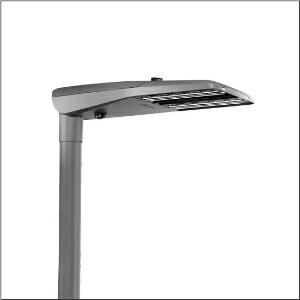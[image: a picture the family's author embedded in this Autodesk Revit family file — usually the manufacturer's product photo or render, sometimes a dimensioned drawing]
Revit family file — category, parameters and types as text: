
# Revit family: streetlight_sl_11_iq_midi___st1_2a_5xc3a61y08me_9d9d
name_source: partatom
category: Lighting Fixtures
units: mm (PartAtom-declared; Revit-internal decimal feet)

## family parameters
Cut with Voids When Loaded = No
Host = Face
Light Source = No
Part Type = Normal
Room Calculation Point = No
Round Connector Dimension = Use Diameter
Shared = No

## types (1)
- --- (1 x LED, 16240 lm, 122.7 W, 2700K)
    Apparent Load = 123 VA
    CIE Flux Codes = 32 70 96 100 100
    Color Rendering = 70
    Color Temperature = 2700K
    Default Elevation = 1800 mm
    Description = Streetlight SL 11 iQ midi, mast luminaire, primary light control with 3 zone facetted reflector, of plastic, silver coated, highly specular, primary optical cover: cover, of PMMA, transparent, light distribution: ST1.2a, light emission: direct distribution, primary light characteristic: asymmetric, installation type: post-top, side-entry, LED, High Power LED, rated luminous flux: 16.240lm, luminous efficacy: 132lm/W, light colour: 727, colour temperature: 2700K, control: presetting dimming logarithmic, Street-Remote, Auto-Match, Temp-Guard, Lumen-Switch, Night-Set, Smart-Wire, Light-Fading, Desk-Remote (wireless, voltage-free reading and setting of iQ features in the workshop via application-optimized NFC function/RFID function), optimised constant luminous flux control (CLO 2.0), with cable H07RN-F 5x 1.5mm², mains connection: 230..240V, AC, 50/60Hz, connection cable pre-assembled, cable length: 12,5m, start of lifetime: 123W, end of service life: 130W, reduction: 56W, luminaire housing, of diecast aluminium, powder-coated, Siteco® metallic grey (DB 702S), please order mast flange separately, inclination adjustable without tools: 0°, 5°, 10°, 15° (post-top) | 0°, -5°, -10°, -15° (side-entry), sealing non-destructively replaceable, multi-level sealing system, length: 780mm, width: 376mm, height: 118mm, mast flange for spigot size: 42mm (side-entry): 5XC10008XM4, 60/48mm (side-entry/post-top): 5XC10108XM2, 76/60mm (side-entry/post-top): 5XC10108XM1, equipment: Power, Smart Interface below and above, protection rating (complete): IP66, insulation class (complete): insulation class II (safety insulation), certification: CE, ENEC, VDE, UKCA, impact resistance: IK09, permissible operating ambient temperature for outdoor applications: -25..+50°C, standard-compliant lighting for roads and squares, Environmental Product Declaration (EPD) tested and certified by an independent institute, packaging unit: 1 piece

Light Distribution: ST1.2a
    Height = 118 mm
    Lamp = 1 x LED
    Lamp Light Flux = 16240 lm
    Lamp Power = 122.7 W
    Lamp count = 1
    Length = 780 mm
    Luminous efficacy = 132 lm/W
    Manufacturer = Siteco
    ModVariant = No
    Model = 5XC3A61Y08ME
    Number of Poles = 1
    OnlyDefault = Yes
    Power Factor = 1
    Product Name = Streetlight SL 11 iQ midi | ST1.2a
    Product group = mast luminaire | pylon top
    ProductGroupID = 6100
    Protection Class = Protection class II
    Protection Degree = IP 66
    RLX_Detail_Level = 1
    RLX_Emergency_Light_Flux = 0 lm
    RLX_Emergency_Type = 0
    RLX_Emergency_Type_DB = No
    RlxData = <blob elided: 69865 chars, md5=5700a3e9>
    Socket = socket
    Standby Power = 0 W
    System Light Flux = 16241 lm
    System Power = 123 W
    Type Comments = factory setting: luminous flux: 100 % | dim-lin: 254 | 553 mA
    Type Image = l_1004429.jpg
    URL = http://relux.com
    VarID = @adj_064371
    Voltage = 0 V
    Weight = 0.00 kg
    Width = 376 mm

## geometry (parser evidence)
native form markers: Blend x4, Sweep x8
no freeform markers — native parametric forms only
